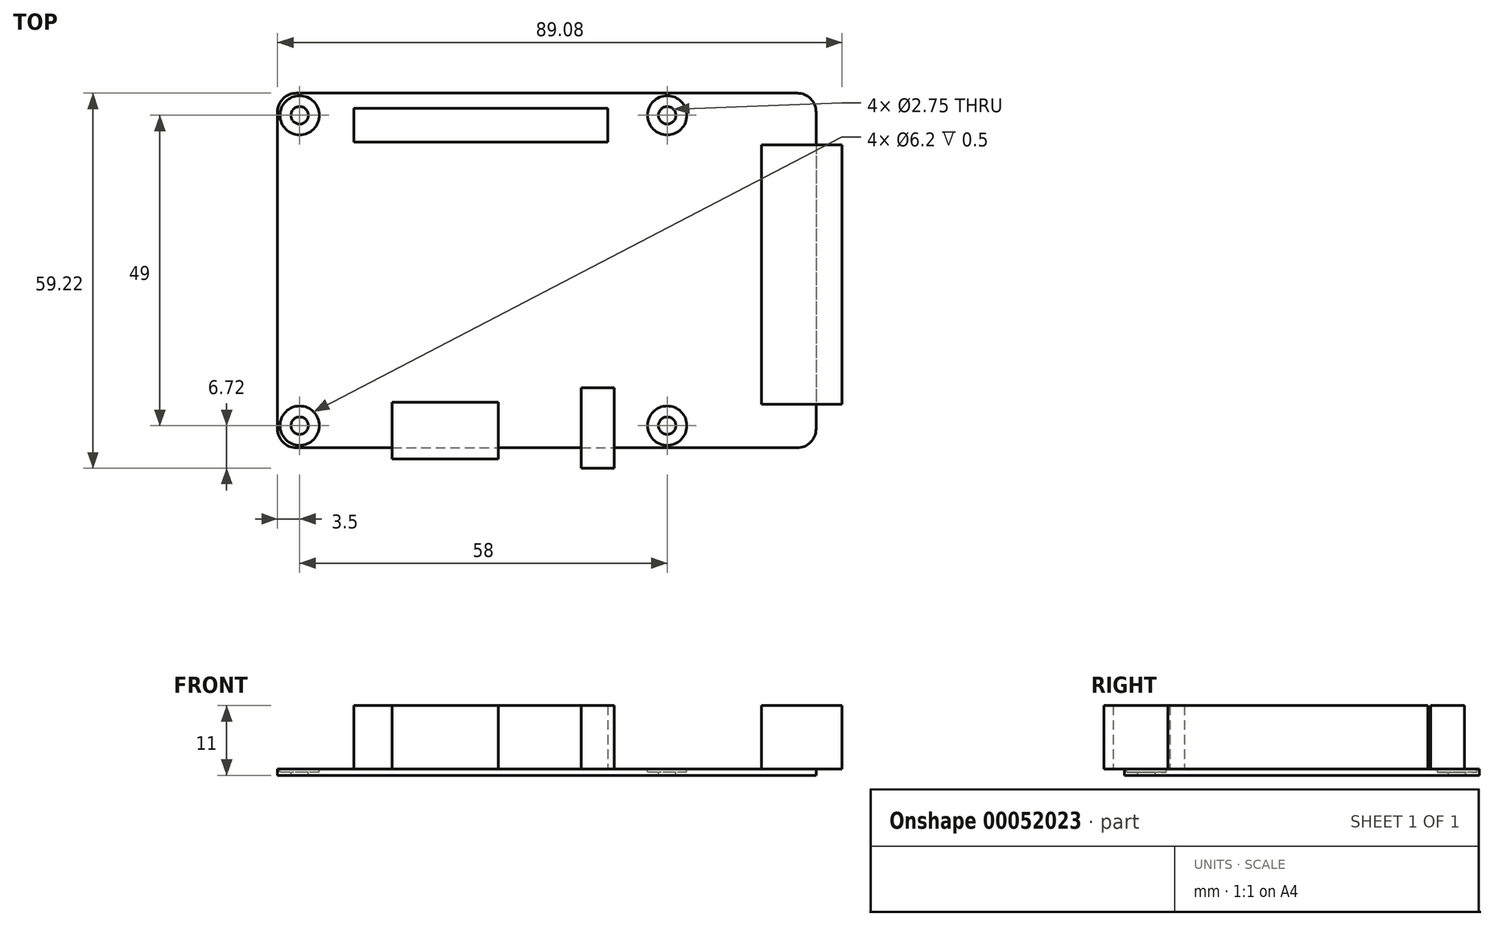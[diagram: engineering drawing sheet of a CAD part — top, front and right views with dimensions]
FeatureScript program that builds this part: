
annotation { "Feature Type Name" : "Feature", "Feature Type Description" : "" }
export const myFeature = defineFeature(function(context is Context, id is Id, definition is map)
    precondition{}
    {
        {
            var Q0;
            Q0=qCreatedBy(makeId("Top.planeOp"),FACE);
            var sketch = newSketch(context, id + "F0", { "sketchPlane" : qUnion([Q0])});
            skLineSegment(sketch, "E0.bottom", {"start": v(-42.5, 28) * mm, "end": v(42.5, 28) * mm});
            skLineSegment(sketch, "E0.top", {"start": v(-42.5, -28) * mm, "end": v(42.5, -28) * mm});
            skLineSegment(sketch, "E0.left", {"start": v(-42.5, 28) * mm, "end": v(-42.5, -28) * mm});
            skLineSegment(sketch, "E0.right", {"start": v(42.5, 28) * mm, "end": v(42.5, -28) * mm});
            skLineSegment(sketch, "E1", {"start": v(-42.5, 28) * mm, "end": v(42.5, -28) * mm});
            skPoint(sketch, "E2", {"position": v(0, 0) * mm});
            skSolve(sketch);
        }
        {
            var Q0;
            Q0=makeQuery(id+"F0.imprint","IMPRINT",FACE,{"disambiguationData":[TD([[makeQuery(id+"F0.imprint","IMPRINT",EDGE,{"derivedFrom":sQuery(id+"F0.wireOp",EDGE,"E0.top")}),1.0]])]});
            var Q1;
            Q1=makeQuery(id+"F0.imprint","IMPRINT",FACE,{"disambiguationData":[TD([[makeQuery(id+"F0.imprint","IMPRINT",EDGE,{"derivedFrom":sQuery(id+"F0.wireOp",EDGE,"E0.bottom")}),-1.0]])]});
            extrude(context, id + "F1", {"entities" : qUnion([Q0, Q1]), "depth" : 1 * mm});
        }
        {
            var Q0;
            Q0=makeQuery(id+"F1.opExtrude","SWEPT_EDGE",EDGE,{"disambiguationData":[OSD([sQuery(id+"F0.wireOp",EDGE,"E0.top"),sQuery(id+"F0.wireOp",EDGE,"E0.left")])]});
            var Q1;
            Q1=makeQuery(id+"F1.opExtrude","SWEPT_EDGE",EDGE,{"disambiguationData":[OSD([sQuery(id+"F0.wireOp",EDGE,"E0.bottom"),sQuery(id+"F0.wireOp",EDGE,"E0.left"),sQuery(id+"F0.wireOp",EDGE,"E1")])]});
            var Q2;
            Q2=makeQuery(id+"F1.opExtrude","SWEPT_EDGE",EDGE,{"disambiguationData":[OSD([sQuery(id+"F0.wireOp",EDGE,"E0.top"),sQuery(id+"F0.wireOp",EDGE,"E0.right"),sQuery(id+"F0.wireOp",EDGE,"E1")])]});
            var Q3;
            Q3=makeQuery(id+"F1.opExtrude","SWEPT_EDGE",EDGE,{"disambiguationData":[OSD([sQuery(id+"F0.wireOp",EDGE,"E0.bottom"),sQuery(id+"F0.wireOp",EDGE,"E0.right")])]});
            fillet(context, id + "F2", {"entities" : qUnion([Q0, Q1, Q2, Q3]), "radius" : 3 * mm, "tangentPropagation" : true, "allowEdgeOverflow" : false});
        }
        {
            var Q0;
            Q0=makeQuery(id+"F1.opExtrude","CAP_FACE",FACE,{"disambiguationData":[OSD([sQuery(id+"F0.wireOp",EDGE,"E0.bottom"),sQuery(id+"F0.wireOp",EDGE,"E0.top"),sQuery(id+"F0.wireOp",EDGE,"E0.left"),sQuery(id+"F0.wireOp",EDGE,"E0.right")])],"isStart":false});
            var sketch = newSketch(context, id + "F3", { "sketchPlane" : qUnion([Q0])});
            skLineSegment(sketch, "E3.bottom", {"start": v(-39, 24.5) * mm, "end": v(19, 24.5) * mm});
            skLineSegment(sketch, "E3.top", {"start": v(-39, -24.5) * mm, "end": v(19, -24.5) * mm});
            skLineSegment(sketch, "E3.left", {"start": v(-39, 24.5) * mm, "end": v(-39, -24.5) * mm});
            skLineSegment(sketch, "E3.right", {"start": v(19, 24.5) * mm, "end": v(19, -24.5) * mm});
            skLineSegment(sketch, "E4", {"start": v(0, 0) * mm, "end": v(19, 0) * mm});
            skPoint(sketch, "E5", {"position": v(19, 0) * mm});
            skSolve(sketch);
        }
        {
            var Q0;
            Q0=sQuery(id+"F3.wireOp",VERTEX,"E3.bottom.start");
            var Q1;
            Q1=sQuery(id+"F3.wireOp",VERTEX,"E3.left.end");
            var Q2;
            Q2=sQuery(id+"F3.wireOp",VERTEX,"E3.top.end");
            var Q3;
            Q3=sQuery(id+"F3.wireOp",VERTEX,"E3.right.start");
            var Q4;
            Q4=makeQuery(id+"F1.opExtrude","SWEPT_BODY",BODY,{"disambiguationData":[OSD([sQuery(id+"F0.wireOp",EDGE,"E0.bottom"),sQuery(id+"F0.wireOp",EDGE,"E0.top"),sQuery(id+"F0.wireOp",EDGE,"E0.left"),sQuery(id+"F0.wireOp",EDGE,"E0.right")])]});
            hole(context, id + "F4", {"style" : HoleStyle.C_BORE, "holeDiameter" : 2.75 * mm, "cBoreDiameter" : 6.2 * mm, "cBoreDepth" : 0.5 * mm, "endStyle" : HoleEndStyle.THROUGH, "locations" : qUnion([Q0, Q1, Q2, Q3]), "scope" : qUnion([Q4])});
        }
        {
            var Q0;
            Q0=makeQuery(id+"F1.opExtrude","CAP_FACE",FACE,{"disambiguationData":[OSD([sQuery(id+"F0.wireOp",EDGE,"E0.bottom"),sQuery(id+"F0.wireOp",EDGE,"E0.top"),sQuery(id+"F0.wireOp",EDGE,"E0.left"),sQuery(id+"F0.wireOp",EDGE,"E0.right")])],"isStart":false});
            var sketch = newSketch(context, id + "F5", { "sketchPlane" : qUnion([Q0])});
            skLineSegment(sketch, "E6.bottom", {"start": v(33.88, 19.86) * mm, "end": v(46.58, 19.86) * mm});
            skLineSegment(sketch, "E6.top", {"start": v(33.88, -21.12) * mm, "end": v(46.58, -21.12) * mm});
            skLineSegment(sketch, "E6.left", {"start": v(33.88, 19.86) * mm, "end": v(33.88, -21.12) * mm});
            skLineSegment(sketch, "E6.right", {"start": v(46.58, 19.86) * mm, "end": v(46.58, -21.12) * mm});
            skLineSegment(sketch, "E7.bottom", {"start": v(-30.47, 25.63) * mm, "end": v(9.64, 25.63) * mm});
            skLineSegment(sketch, "E7.top", {"start": v(-30.47, 20.3) * mm, "end": v(9.64, 20.3) * mm});
            skLineSegment(sketch, "E7.left", {"start": v(-30.47, 25.63) * mm, "end": v(-30.47, 20.3) * mm});
            skLineSegment(sketch, "E7.right", {"start": v(9.64, 25.63) * mm, "end": v(9.64, 20.3) * mm});
            skLineSegment(sketch, "E8.bottom", {"start": v(-7.67, -29.78) * mm, "end": v(-24.41, -29.78) * mm});
            skLineSegment(sketch, "E8.top", {"start": v(-7.67, -20.83) * mm, "end": v(-24.41, -20.83) * mm});
            skLineSegment(sketch, "E8.left", {"start": v(-7.67, -29.78) * mm, "end": v(-7.67, -20.83) * mm});
            skLineSegment(sketch, "E8.right", {"start": v(-24.41, -29.78) * mm, "end": v(-24.41, -20.83) * mm});
            skLineSegment(sketch, "E9.bottom", {"start": v(5.46, -18.52) * mm, "end": v(10.65, -18.52) * mm});
            skLineSegment(sketch, "E9.top", {"start": v(5.46, -31.22) * mm, "end": v(10.65, -31.22) * mm});
            skLineSegment(sketch, "E9.left", {"start": v(5.46, -18.52) * mm, "end": v(5.46, -31.22) * mm});
            skLineSegment(sketch, "E9.right", {"start": v(10.65, -18.52) * mm, "end": v(10.65, -31.22) * mm});
            skSolve(sketch);
        }
        {
            var Q0;
            Q0=makeQuery(id+"F5.imprint","IMPRINT",FACE,{"disambiguationData":[TD([[makeQuery(id+"F5.imprint","IMPRINT",EDGE,{"derivedFrom":sQuery(id+"F5.wireOp",EDGE,"E7.bottom")}),-1.0]])]});
            var Q1;
            {var subQ0=sQuery(id+"F5.wireOp",EDGE,"E6.left");Q1=makeQuery(id+"F5.imprint","IMPRINT",FACE,{"disambiguationData":[TD([[makeQuery(id+"F5.imprint","IMPRINT",EDGE,{"derivedFrom":subQ0}),1.0]])]});}
            var Q2;
            {var subQ0=sQuery(id+"F5.wireOp",EDGE,"E6.right");Q2=makeQuery(id+"F5.imprint","IMPRINT",FACE,{"disambiguationData":[TD([[makeQuery(id+"F5.imprint","IMPRINT",EDGE,{"derivedFrom":subQ0}),-1.0]])]});}
            var Q3;
            {var subQ0=sQuery(id+"F5.wireOp",EDGE,"E8.top");Q3=makeQuery(id+"F5.imprint","IMPRINT",FACE,{"disambiguationData":[TD([[makeQuery(id+"F5.imprint","IMPRINT",EDGE,{"derivedFrom":subQ0}),1.0]])]});}
            var Q4;
            {var subQ0=sQuery(id+"F5.wireOp",EDGE,"E8.bottom");Q4=makeQuery(id+"F5.imprint","IMPRINT",FACE,{"disambiguationData":[TD([[makeQuery(id+"F5.imprint","IMPRINT",EDGE,{"derivedFrom":subQ0}),-1.0]])]});}
            var Q5;
            {var subQ0=sQuery(id+"F5.wireOp",EDGE,"E9.bottom");Q5=makeQuery(id+"F5.imprint","IMPRINT",FACE,{"disambiguationData":[TD([[makeQuery(id+"F5.imprint","IMPRINT",EDGE,{"derivedFrom":subQ0}),-1.0]])]});}
            var Q6;
            {var subQ0=sQuery(id+"F5.wireOp",EDGE,"E9.top");Q6=makeQuery(id+"F5.imprint","IMPRINT",FACE,{"disambiguationData":[TD([[makeQuery(id+"F5.imprint","IMPRINT",EDGE,{"derivedFrom":subQ0}),1.0]])]});}
            extrude(context, id + "F6", {"entities" : qUnion([Q0, Q1, Q2, Q3, Q4, Q5, Q6]), "operationType" : NewBodyOperationType.ADD, "depth" : 10 * mm});
        }
    });
